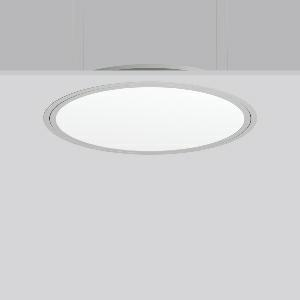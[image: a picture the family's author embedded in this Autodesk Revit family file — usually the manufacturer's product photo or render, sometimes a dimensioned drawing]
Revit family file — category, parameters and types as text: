
# Revit family: triona_round_e_312383_004_12_1df4
name_source: partatom
category: Lighting Fixtures
units: mm (PartAtom-declared; Revit-internal decimal feet)

## family parameters
Cut with Voids When Loaded = No
Host = Face
Light Source = No
Part Type = Normal
Room Calculation Point = No
Round Connector Dimension = Use Diameter
Shared = No

## types (1)
- TRIONA round E (1 x LED Modul 830, 6450 lm, 3000)
    Apparent Load = 70 VA
    CIE Flux Codes = 49 80 96 100 100
    Color Rendering = 80
    Color Temperature = 3000
    Default Elevation = 1800 mm
    Description = Series: TRIONA round
Decorative round LED recessed surface luminaire. Cover made of sheet steel, powder-coated. Frame made of aluminium, powder-coated. Recessed ring: aluminium extrusion profile, powder coated. Light emission through a diffuser: plastic, opal. Lightguide and diffuser made of non-yellowing plastic (PMMA). Lateral light emission (RZB SIDELITE technology) for above-average homogeneous light distribution. Suitable for installation in cavity ceilings. Tool-free mounting system thanks to the rocker arm mechanism (patent pending). Electronic ballast included. Very easy installation thanks to Plug+Play connection. 
Colour: silver, matt (approx. RAL 9006)
Diameter: 725 mm
Height: 2 mm
Cut-out diameter: 702 mm
Recess height: 100 mm
Luminaire: recess height: 89 mm
Lamp: LED
Socket: without socket
Colour temperature: 3000K
Colour rendering index (CRI): 80
System power: 70 W
Rated luminous flux: 6450 lm
Luminous efficiency: 92 lm/W
Control gear: Converter, dimmable, DALI
Protection class: I
Type of protection: IP 40
    Height = 0 mm  [stored 0 ft]
    Lamp = 1 x LED Modul 830
    Lamp Light Flux = 6450 lm
    Lamp count = 1
    Length = 725 mm
    Lifetime = 50000 h
    Luminous efficacy = 92 lm/W
    Manufacturer = RZB
    ModVariant = No
    Model = 312383.004.12
    Mounting Place = Ceiling
    Mounting Type = Recessed
    Number of Poles = 1
    OnlyDefault = Yes
    Power Factor = 1
    Product Name = TRIONA round E
    Product group = Recessed modular luminaires
    ProductGroupID = 406
    Protection Class = Protection class I
    Protection Degree = IP 20
    RLX_Detail_Level = 1
    RLX_Emergency_Light_Flux = 0 lm
    RLX_Emergency_Type = 0
    RLX_Emergency_Type_DB = No
    RlxData = <blob elided: 35597 chars, md5=e7d8ac7d>
    Socket = socket
    Standby Power = 0 W
    System Light Flux = 6450 lm
    System Power = 70 W
    Type Comments = Product without accessories
    Type Image = 312383.004.12.jpg
    URL = http://relux.com
    VarID = ---
    Voltage = 230 V
    Voltage Range = 220-240 V
    Weight = 0.00 kg
    Width = 0 mm  [stored 0 ft]

note: [stored X ft] marks values corroborated as IEEE doubles in the binary element streams (Revit-internal decimal feet)

## geometry (parser evidence)
native form markers: Blend x4, Sweep x10
no freeform markers — native parametric forms only
